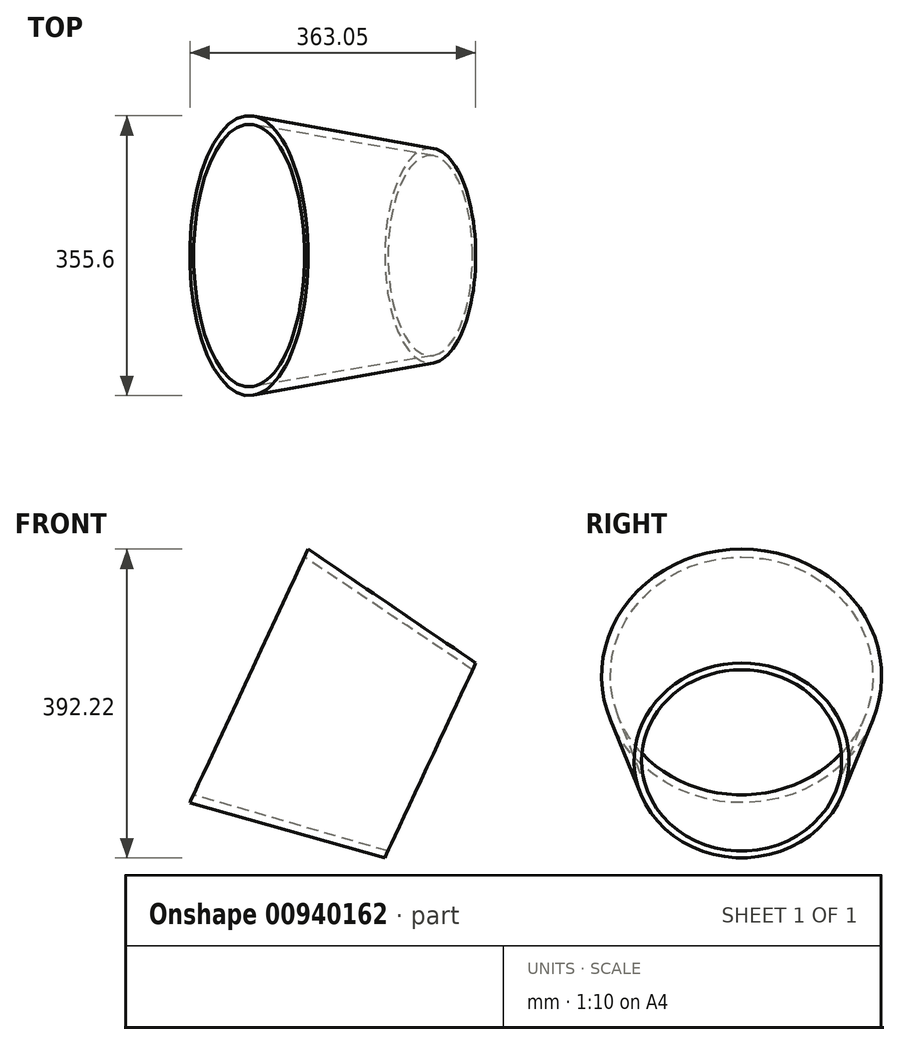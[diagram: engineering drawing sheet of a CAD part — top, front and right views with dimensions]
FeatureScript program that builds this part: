
annotation { "Feature Type Name" : "Feature", "Feature Type Description" : "" }
export const myFeature = defineFeature(function(context is Context, id is Id, definition is map)
    precondition{}
    {
        {
            var Q0;
            Q0=qCreatedBy(makeId("Front.planeOp"),FACE);
            var sketch = newSketch(context, id + "F0", { "sketchPlane" : qUnion([Q0])});
            skLineSegment(sketch, "E0", {"start": v(-230.2, 107.35) * mm, "end": v(0, 0) * mm, "construction": true});
            skLineSegment(sketch, "E1", {"start": v(-85.76, -156.2) * mm, "end": v(161.89, -226.13) * mm});
            skLineSegment(sketch, "E2", {"start": v(161.89, -226.13) * mm, "end": v(165.86, -217.61) * mm});
            skLineSegment(sketch, "E3", {"start": v(165.86, -217.61) * mm, "end": v(-81.03, -146.06) * mm});
            skLineSegment(sketch, "E4", {"start": v(-81.03, -146.06) * mm, "end": v(-85.76, -156.2) * mm});
            skSolve(sketch);
        }
        {
            var Q0;
            Q0=qSketchRegion(id+"F0",true);
            var Q1;
            Q1=sQuery(id+"F0.wireOp",EDGE,"E0");
            revolve(context, id + "F1", {"entities" : qUnion([Q0]), "axis" : qUnion([Q1]), "revolveType" : RevolveType.FULL});
        }
    });
